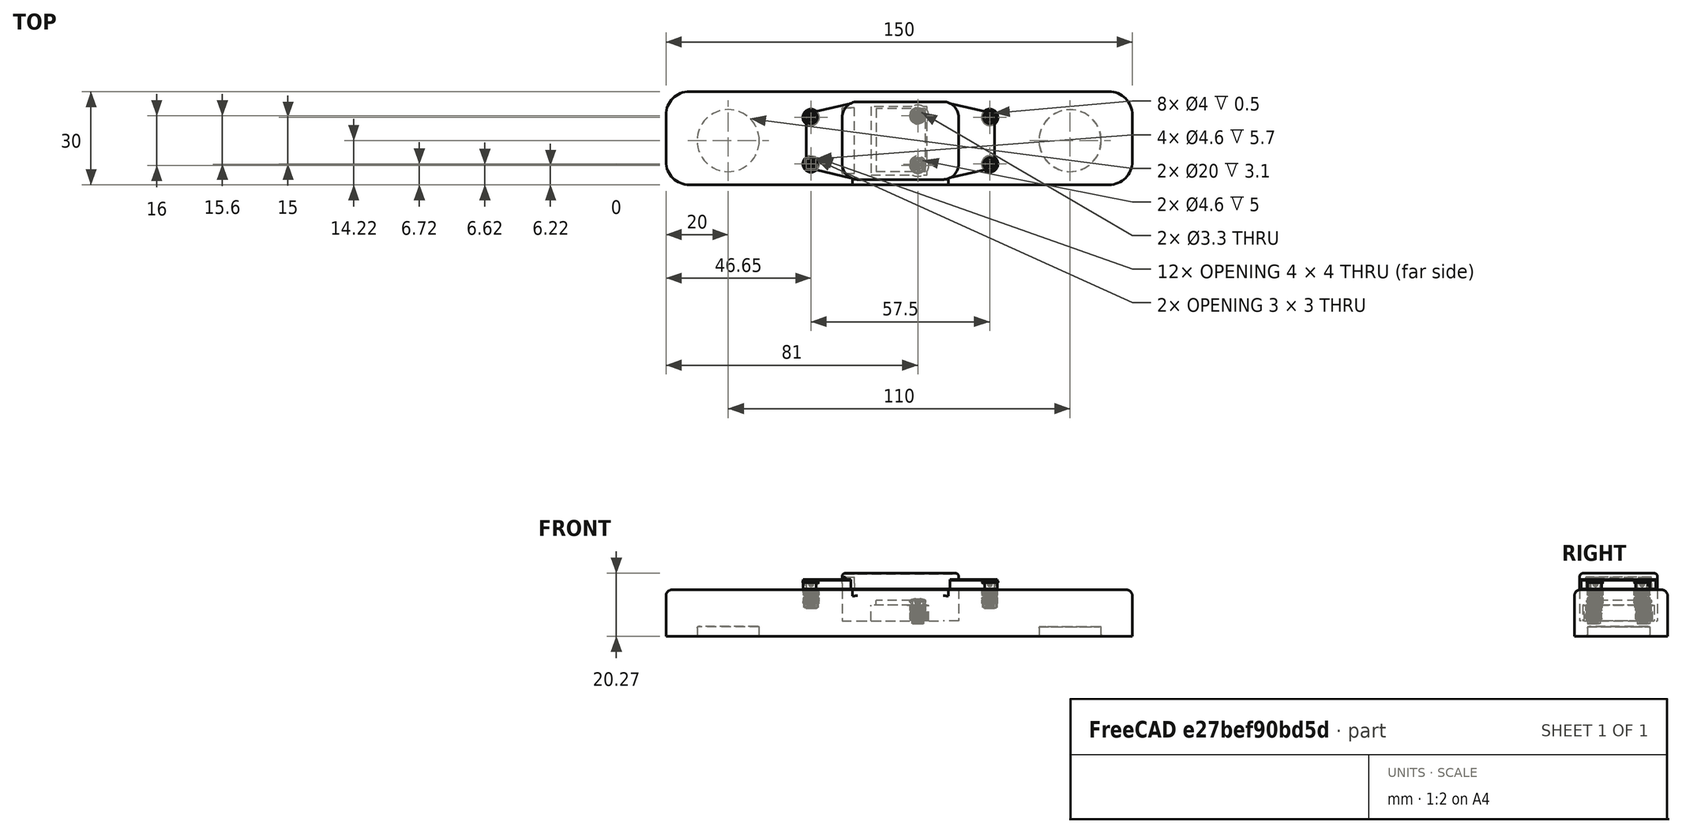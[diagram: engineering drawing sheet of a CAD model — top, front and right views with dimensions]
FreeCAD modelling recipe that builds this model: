
FCSTD DOCUMENT  (FreeCAD 0.20R29603 (Git))
Label: MMI Assembly
License: All rights reserved
LicenseURL: http://en.wikipedia.org/wiki/All_rights_reserved
objects: App::FeaturePython×30, Part::FeaturePython×18
note: 18 computed .brp shape members not serialized (recipe doc carries the construction recipe); baked Part::Feature solids carry a one-line shape summary decoded from their .brp

FEATURE [Part::FeaturePython] b_Sensor_Holder_001_  label="Sensor Holder_001"  # a2plus imported part (geometry in sourceFile) (typed FeaturePython)
  a2p_Version = 0.4.60n
  fixedPosition = true
  objectType = a2pPart
  sourceFile = .\Sensor Holder.FCStd
  subassemblyImport = false
  timeLastImport = 1.68601e+09
  updateColors = true
FEATURE [Part::FeaturePython] b_M3_Heat_Insert_001_  label="M3 Heat Insert_001"  # a2plus imported part (geometry in sourceFile) (typed FeaturePython)
  Placement = pos=(6.00013,7.99989,4) rot=(0,0,1;0rad)
  a2p_Version = 0.4.60n
  fixedPosition = false
  objectType = a2pPart
  sourceFile = .\M3 Heat Insert.FCStd
  subassemblyImport = false
  timeLastImport = 1.68601e+09
  updateColors = true
FEATURE [App::FeaturePython] centerOfMass_001  label="centerOfMass_001__M3 Heat Insert_001"  # a2plus constraint (typed FeaturePython)
  Object1 = b_Sensor_Holder_001_
  Object2 = b_M3_Heat_Insert_001_
  ParentTreeObject = -> b_Sensor_Holder_001_
  SubElement1 = Edge144
  SubElement2 = Edge31
  Suppressed = false
  Type = CenterOfMass
  directionConstraint = 0
  lockRotation = false
  offset = 0
FEATURE [App::FeaturePython] centerOfMass_001_mirror  label="centerOfMass_001__Sensor Holder_001"  # a2plus constraint (typed FeaturePython)
  Object1 = b_Sensor_Holder_001_
  Object2 = b_M3_Heat_Insert_001_
  ParentTreeObject = -> b_M3_Heat_Insert_001_
  SubElement1 = Edge144
  SubElement2 = Edge31
  Suppressed = false
  Type = CenterOfMass
  directionConstraint = 0
  lockRotation = false
  offset = 0
FEATURE [Part::FeaturePython] b_M3_Heat_Insert_001_001  label="M3 Heat Insert_002"  # a2plus imported part (geometry in sourceFile) (typed FeaturePython)
  Placement = pos=(6.00013,-8.00011,4) rot=(0,0,1;0rad)
  a2p_Version = 0.4.60n
  fixedPosition = false
  objectType = a2pPart
  sourceFile = .\M3 Heat Insert.FCStd
  subassemblyImport = false
  timeLastImport = 1.68601e+09
  updateColors = true
FEATURE [App::FeaturePython] centerOfMass_002  label="centerOfMass_002__Sensor Holder_001"  # a2plus constraint (typed FeaturePython)
  Object1 = b_M3_Heat_Insert_001_001
  Object2 = b_Sensor_Holder_001_
  ParentTreeObject = -> b_M3_Heat_Insert_001_001
  SubElement1 = Edge31
  SubElement2 = Edge145
  Suppressed = false
  Type = CenterOfMass
  directionConstraint = 0
  lockRotation = false
  offset = 0
FEATURE [App::FeaturePython] centerOfMass_002_mirror  label="centerOfMass_002__M3 Heat Insert_002"  # a2plus constraint (typed FeaturePython)
  Object1 = b_M3_Heat_Insert_001_001
  Object2 = b_Sensor_Holder_001_
  ParentTreeObject = -> b_Sensor_Holder_001_
  SubElement1 = Edge31
  SubElement2 = Edge145
  Suppressed = false
  Type = CenterOfMass
  directionConstraint = 0
  lockRotation = false
  offset = 0
FEATURE [Part::FeaturePython] b_M3_Heat_Insert_001_002  label="M3 Heat Insert_003"  # a2plus imported part (geometry in sourceFile) (typed FeaturePython)
  Placement = pos=(-28.3499,7.49989,9) rot=(0,0,1;0rad)
  a2p_Version = 0.4.60n
  fixedPosition = false
  objectType = a2pPart
  sourceFile = .\M3 Heat Insert.FCStd
  subassemblyImport = false
  timeLastImport = 1.68601e+09
  updateColors = true
FEATURE [App::FeaturePython] centerOfMass_003  label="centerOfMass_003__Sensor Holder_001"  # a2plus constraint (typed FeaturePython)
  Object1 = b_M3_Heat_Insert_001_002
  Object2 = b_Sensor_Holder_001_
  ParentTreeObject = -> b_M3_Heat_Insert_001_002
  SubElement1 = Edge31
  SubElement2 = Edge19
  Suppressed = false
  Type = CenterOfMass
  directionConstraint = 0
  lockRotation = false
  offset = 0
FEATURE [App::FeaturePython] centerOfMass_003_mirror  label="centerOfMass_003__M3 Heat Insert_003"  # a2plus constraint (typed FeaturePython)
  Object1 = b_M3_Heat_Insert_001_002
  Object2 = b_Sensor_Holder_001_
  ParentTreeObject = -> b_Sensor_Holder_001_
  SubElement1 = Edge31
  SubElement2 = Edge19
  Suppressed = false
  Type = CenterOfMass
  directionConstraint = 0
  lockRotation = false
  offset = 0
FEATURE [Part::FeaturePython] b_M3_Heat_Insert_001_003  label="M3 Heat Insert_004"  # a2plus imported part (geometry in sourceFile) (typed FeaturePython)
  Placement = pos=(-28.3499,-7.50011,9) rot=(0,0,1;0rad)
  a2p_Version = 0.4.60n
  fixedPosition = false
  objectType = a2pPart
  sourceFile = .\M3 Heat Insert.FCStd
  subassemblyImport = false
  timeLastImport = 1.68601e+09
  updateColors = true
FEATURE [Part::FeaturePython] b_M3_Heat_Insert_001_004  label="M3 Heat Insert_005"  # a2plus imported part (geometry in sourceFile) (typed FeaturePython)
  Placement = pos=(29.1501,-7.50011,9) rot=(0,0,1;0rad)
  a2p_Version = 0.4.60n
  fixedPosition = false
  objectType = a2pPart
  sourceFile = .\M3 Heat Insert.FCStd
  subassemblyImport = false
  timeLastImport = 1.68601e+09
  updateColors = true
FEATURE [App::FeaturePython] centerOfMass_005  label="centerOfMass_005__Sensor Holder_001"  # a2plus constraint (typed FeaturePython)
  Object1 = b_M3_Heat_Insert_001_004
  Object2 = b_Sensor_Holder_001_
  ParentTreeObject = -> b_M3_Heat_Insert_001_004
  SubElement1 = Edge31
  SubElement2 = Edge18
  Suppressed = false
  Type = CenterOfMass
  directionConstraint = 0
  lockRotation = false
  offset = 0
FEATURE [App::FeaturePython] centerOfMass_005_mirror  label="centerOfMass_005__M3 Heat Insert_005"  # a2plus constraint (typed FeaturePython)
  Object1 = b_M3_Heat_Insert_001_004
  Object2 = b_Sensor_Holder_001_
  ParentTreeObject = -> b_Sensor_Holder_001_
  SubElement1 = Edge31
  SubElement2 = Edge18
  Suppressed = false
  Type = CenterOfMass
  directionConstraint = 0
  lockRotation = false
  offset = 0
FEATURE [Part::FeaturePython] b_M3_Heat_Insert_001_005  label="M3 Heat Insert_006"  # a2plus imported part (geometry in sourceFile) (typed FeaturePython)
  Placement = pos=(29.1501,7.49989,9) rot=(0,0,1;0rad)
  a2p_Version = 0.4.60n
  fixedPosition = false
  objectType = a2pPart
  sourceFile = .\M3 Heat Insert.FCStd
  subassemblyImport = false
  timeLastImport = 1.68601e+09
  updateColors = true
FEATURE [App::FeaturePython] centerOfMass_006  label="centerOfMass_006__Sensor Holder_001"  # a2plus constraint (typed FeaturePython)
  Object1 = b_M3_Heat_Insert_001_005
  Object2 = b_Sensor_Holder_001_
  ParentTreeObject = -> b_M3_Heat_Insert_001_005
  SubElement1 = Edge31
  SubElement2 = Edge20
  Suppressed = false
  Type = CenterOfMass
  directionConstraint = 0
  lockRotation = false
  offset = 0
FEATURE [App::FeaturePython] centerOfMass_006_mirror  label="centerOfMass_006__M3 Heat Insert_006"  # a2plus constraint (typed FeaturePython)
  Object1 = b_M3_Heat_Insert_001_005
  Object2 = b_Sensor_Holder_001_
  ParentTreeObject = -> b_Sensor_Holder_001_
  SubElement1 = Edge31
  SubElement2 = Edge20
  Suppressed = false
  Type = CenterOfMass
  directionConstraint = 0
  lockRotation = false
  offset = 0
FEATURE [Part::FeaturePython] b_Sensor_Holder_Cap_001_  label="Sensor Holder Cap_001"  # a2plus imported part (geometry in sourceFile) (typed FeaturePython)
  Placement = pos=(0.4,9.94825e-09,15.2703) rot=(0,0,1;0rad)
  a2p_Version = 0.4.60n
  fixedPosition = false
  objectType = a2pPart
  sourceFile = .\Sensor Holder Cap.FCStd
  subassemblyImport = false
  timeLastImport = 1.68601e+09
  updateColors = true
FEATURE [App::FeaturePython] axisCoincident_001  label="axisCoincident_001__Sensor Holder Cap_001"  # a2plus constraint (typed FeaturePython)
  Object1 = b_Sensor_Holder_001_
  Object2 = b_Sensor_Holder_Cap_001_
  ParentTreeObject = -> b_Sensor_Holder_001_
  SubElement1 = Edge17
  SubElement2 = Edge148
  Suppressed = false
  Type = axial
  directionConstraint = 0
  lockRotation = false
FEATURE [App::FeaturePython] axisCoincident_001_mirror  label="axisCoincident_001__Sensor Holder_001"  # a2plus constraint (typed FeaturePython)
  Object1 = b_Sensor_Holder_001_
  Object2 = b_Sensor_Holder_Cap_001_
  ParentTreeObject = -> b_Sensor_Holder_Cap_001_
  SubElement1 = Edge17
  SubElement2 = Edge148
  Suppressed = false
  Type = axial
  directionConstraint = 0
  lockRotation = false
FEATURE [Part::FeaturePython] b_MPU6050_PCBA_001_  label="MPU6050_PCBA_Body_001"  # a2plus imported part (geometry in sourceFile) (typed FeaturePython)
  Placement = pos=(0.8,0.2,10) rot=(0,0,-1;1.5708rad)
  a2p_Version = 0.4.60n
  fixedPosition = false
  objectType = a2pPart
  sourceFile = .\MPU6050_PCBA.FCStd
  sourcePart = Body
  subassemblyImport = false
  timeLastImport = 1.68601e+09
  updateColors = true
FEATURE [App::FeaturePython] centerOfMass_004  label="centerOfMass_004__M3 Heat Insert_001"  # a2plus constraint (typed FeaturePython)
  Object1 = b_MPU6050_PCBA_001_
  Object2 = b_M3_Heat_Insert_001_
  ParentTreeObject = -> b_MPU6050_PCBA_001_
  SubElement1 = Edge12
  SubElement2 = Edge31
  Suppressed = false
  Type = CenterOfMass
  directionConstraint = 0
  lockRotation = false
  offset = 0
FEATURE [App::FeaturePython] centerOfMass_004_mirror  label="centerOfMass_004__MPU6050_PCBA_Body_001"  # a2plus constraint (typed FeaturePython)
  Object1 = b_MPU6050_PCBA_001_
  Object2 = b_M3_Heat_Insert_001_
  ParentTreeObject = -> b_M3_Heat_Insert_001_
  SubElement1 = Edge12
  SubElement2 = Edge31
  Suppressed = false
  Type = CenterOfMass
  directionConstraint = 0
  lockRotation = false
  offset = 0
FEATURE [Part::FeaturePython] Screw  label="M3x5-Screw"  # Fasteners workbench fastener (typed FeaturePython)
  Placement = pos=(6,8,11.5) rot=(0,0,1;0rad)
  baseObject = -> b_MPU6050_PCBA_001_ [Edge15]
  diameter = 4
  invert = false
  leftHanded = false
  length = 1
  lengthCustom = 5
  matchOuter = false
  offset = 0
  thread = false
  type = 48
FEATURE [Part::FeaturePython] Screw001  label="M3x6-Screw"  # Fasteners workbench fastener (typed FeaturePython)
  Placement = pos=(6,-7.6,11.5) rot=(0,0,1;0rad)
  baseObject = -> b_MPU6050_PCBA_001_ [Edge16]
  diameter = 4
  invert = false
  leftHanded = false
  length = 2
  lengthCustom = 6
  matchOuter = false
  offset = 0
  thread = false
  type = 48
FEATURE [Part::FeaturePython] Screw006  label="M3x5-Screw005"  # Fasteners workbench fastener (typed FeaturePython)
  Placement = pos=(-28.35,-7.5,17.7703) rot=(0,0,1;0rad)
  baseObject = -> b_Sensor_Holder_Cap_001_ [Edge155]
  diameter = 4
  invert = true
  leftHanded = false
  length = 1
  lengthCustom = 5
  matchOuter = false
  offset = 0
  thread = false
  type = 48
FEATURE [Part::FeaturePython] Screw008  label="M3x5-Screw006"  # Fasteners workbench fastener (typed FeaturePython)
  Placement = pos=(29.15,-7.5,17.7703) rot=(0,0,1;0rad)
  baseObject = -> b_Sensor_Holder_Cap_001_ [Edge143]
  diameter = 4
  invert = true
  leftHanded = false
  length = 1
  lengthCustom = 5
  matchOuter = false
  offset = 0
  thread = false
  type = 48
FEATURE [Part::FeaturePython] Screw009  label="M3x5-Screw007"  # Fasteners workbench fastener (typed FeaturePython)
  Placement = pos=(29.15,7.5,17.7703) rot=(0,0,1;0rad)
  baseObject = -> b_Sensor_Holder_Cap_001_ [Edge133]
  diameter = 4
  invert = true
  leftHanded = false
  length = 1
  lengthCustom = 5
  matchOuter = false
  offset = 0
  thread = false
  type = 48
FEATURE [Part::FeaturePython] Screw010  label="M3x5-Screw004"  # Fasteners workbench fastener (typed FeaturePython)
  Placement = pos=(-28.3497,7.5,17.7703) rot=(0,0,1;0rad)
  baseObject = -> b_Sensor_Holder_Cap_001_ [Edge186]
  diameter = 4
  invert = true
  leftHanded = false
  length = 1
  lengthCustom = 5
  matchOuter = false
  offset = 0
  thread = false
  type = 48
FEATURE [Part::FeaturePython] b_Sensor_Holder_Cap_WH_001_  label="Sensor Holder Cap WH_001"  # a2plus imported part (geometry in sourceFile) (typed FeaturePython)
  Placement = pos=(0.4,0,15) rot=(0,0,1;0rad)
  a2p_Version = 0.4.60n
  fixedPosition = false
  objectType = a2pPart
  sourceFile = .\Sensor Holder Cap WH.FCStd
  subassemblyImport = false
  timeLastImport = 1.68602e+09
  updateColors = true
FEATURE [App::FeaturePython] planesParallel_001  label="planesParallel_001__Sensor Holder Cap WH_001"  # a2plus constraint (typed FeaturePython)
  Object1 = b_M3_Heat_Insert_001_003
  Object2 = b_Sensor_Holder_Cap_WH_001_
  ParentTreeObject = -> b_M3_Heat_Insert_001_003
  SubElement1 = Face1
  SubElement2 = Face83
  Suppressed = false
  Type = planesParallel
  directionConstraint = 0
FEATURE [App::FeaturePython] planesParallel_001_mirror  label="planesParallel_001__M3 Heat Insert_004"  # a2plus constraint (typed FeaturePython)
  Object1 = b_M3_Heat_Insert_001_003
  Object2 = b_Sensor_Holder_Cap_WH_001_
  ParentTreeObject = -> b_Sensor_Holder_Cap_WH_001_
  SubElement1 = Face1
  SubElement2 = Face83
  Suppressed = false
  Type = planesParallel
  directionConstraint = 0
FEATURE [App::FeaturePython] axisCoincident_002  label="axisCoincident_002__Sensor Holder_001"  # a2plus constraint (typed FeaturePython)
  Object1 = b_Sensor_Holder_Cap_WH_001_
  Object2 = b_Sensor_Holder_001_
  ParentTreeObject = -> b_Sensor_Holder_Cap_WH_001_
  SubElement1 = Edge96
  SubElement2 = Edge20
  Suppressed = false
  Type = axial
  directionConstraint = 0
  lockRotation = false
FEATURE [App::FeaturePython] axisCoincident_002_mirror  label="axisCoincident_002__Sensor Holder Cap WH_001"  # a2plus constraint (typed FeaturePython)
  Object1 = b_Sensor_Holder_Cap_WH_001_
  Object2 = b_Sensor_Holder_001_
  ParentTreeObject = -> b_Sensor_Holder_001_
  SubElement1 = Edge96
  SubElement2 = Edge20
  Suppressed = false
  Type = axial
  directionConstraint = 0
  lockRotation = false
FEATURE [App::FeaturePython] pointIdentity_001  label="pointIdentity_001__Sensor Holder_001"  # a2plus constraint (typed FeaturePython)
  Object1 = b_Sensor_Holder_Cap_WH_001_
  Object2 = b_Sensor_Holder_001_
  ParentTreeObject = -> b_Sensor_Holder_Cap_WH_001_
  SubElement1 = Edge140
  SubElement2 = Edge20
  Suppressed = false
  Type = pointIdentity
FEATURE [App::FeaturePython] pointIdentity_001_mirror  label="pointIdentity_001__Sensor Holder Cap WH_001"  # a2plus constraint (typed FeaturePython)
  Object1 = b_Sensor_Holder_Cap_WH_001_
  Object2 = b_Sensor_Holder_001_
  ParentTreeObject = -> b_Sensor_Holder_001_
  SubElement1 = Edge140
  SubElement2 = Edge20
  Suppressed = false
  Type = pointIdentity
FEATURE [Part::FeaturePython] b_Nedymium_Magnet_OD20mm_H3mm_001_  label="Nedymium Magnet OD20mm H3mm_001"  # a2plus imported part (geometry in sourceFile) (typed FeaturePython)
  Placement = pos=(-55,7.33426e-10,0.12) rot=(0,0,1;0rad)
  a2p_Version = 0.4.60n
  fixedPosition = false
  objectType = a2pPart
  sourceFile = .\Nedymium Magnet OD20mm H3mm.FCStd
  subassemblyImport = false
  timeLastImport = 1.6863e+09
  updateColors = true
FEATURE [App::FeaturePython] axisCoincident_003  label="axisCoincident_003__Sensor Holder_001"  # a2plus constraint (typed FeaturePython)
  Object1 = b_Nedymium_Magnet_OD20mm_H3mm_001_
  Object2 = b_Sensor_Holder_001_
  ParentTreeObject = -> b_Nedymium_Magnet_OD20mm_H3mm_001_
  SubElement1 = Edge2
  SubElement2 = Face61
  Suppressed = false
  Type = axial
  directionConstraint = 1
  lockRotation = false
FEATURE [App::FeaturePython] axisCoincident_003_mirror  label="axisCoincident_003__Nedymium Magnet OD20mm H3mm_001"  # a2plus constraint (typed FeaturePython)
  Object1 = b_Nedymium_Magnet_OD20mm_H3mm_001_
  Object2 = b_Sensor_Holder_001_
  ParentTreeObject = -> b_Sensor_Holder_001_
  SubElement1 = Edge2
  SubElement2 = Face61
  Suppressed = false
  Type = axial
  directionConstraint = 1
  lockRotation = false
FEATURE [App::FeaturePython] pointIdentity_002  label="pointIdentity_002__Sensor Holder_001"  # a2plus constraint (typed FeaturePython)
  Object1 = b_Nedymium_Magnet_OD20mm_H3mm_001_
  Object2 = b_Sensor_Holder_001_
  ParentTreeObject = -> b_Nedymium_Magnet_OD20mm_H3mm_001_
  SubElement1 = Edge3
  SubElement2 = Edge141
  Suppressed = false
  Type = pointIdentity
FEATURE [App::FeaturePython] pointIdentity_002_mirror  label="pointIdentity_002__Nedymium Magnet OD20mm H3mm_001"  # a2plus constraint (typed FeaturePython)
  Object1 = b_Nedymium_Magnet_OD20mm_H3mm_001_
  Object2 = b_Sensor_Holder_001_
  ParentTreeObject = -> b_Sensor_Holder_001_
  SubElement1 = Edge3
  SubElement2 = Edge141
  Suppressed = false
  Type = pointIdentity
FEATURE [Part::FeaturePython] b_Nedymium_Magnet_OD20mm_H3mm_001_001  label="Nedymium Magnet OD20mm H3mm_002"  # a2plus imported part (geometry in sourceFile) (typed FeaturePython)
  Placement = pos=(55,-2.32187e-08,0.100006) rot=(0,0,1;0rad)
  a2p_Version = 0.4.60n
  fixedPosition = false
  objectType = a2pPart
  sourceFile = .\Nedymium Magnet OD20mm H3mm.FCStd
  subassemblyImport = false
  timeLastImport = 1.6863e+09
  updateColors = true
FEATURE [App::FeaturePython] axisCoincident_004  label="axisCoincident_004__Sensor Holder_001"  # a2plus constraint (typed FeaturePython)
  Object1 = b_Nedymium_Magnet_OD20mm_H3mm_001_001
  Object2 = b_Sensor_Holder_001_
  ParentTreeObject = -> b_Nedymium_Magnet_OD20mm_H3mm_001_001
  SubElement1 = Face1
  SubElement2 = Face62
  Suppressed = false
  Type = axial
  directionConstraint = 0
  lockRotation = false
FEATURE [App::FeaturePython] axisCoincident_004_mirror  label="axisCoincident_004__Nedymium Magnet OD20mm H3mm_002"  # a2plus constraint (typed FeaturePython)
  Object1 = b_Nedymium_Magnet_OD20mm_H3mm_001_001
  Object2 = b_Sensor_Holder_001_
  ParentTreeObject = -> b_Sensor_Holder_001_
  SubElement1 = Face1
  SubElement2 = Face62
  Suppressed = false
  Type = axial
  directionConstraint = 0
  lockRotation = false
FEATURE [App::FeaturePython] pointOnPlane_001  label="pointOnPlane_001__Sensor Holder_001"  # a2plus constraint (typed FeaturePython)
  Object1 = b_Nedymium_Magnet_OD20mm_H3mm_001_001
  Object2 = b_Sensor_Holder_001_
  ParentTreeObject = -> b_Nedymium_Magnet_OD20mm_H3mm_001_001
  SubElement1 = Edge7
  SubElement2 = Face66
  Suppressed = false
  Type = pointOnPlane
  offset = 0
FEATURE [App::FeaturePython] pointOnPlane_001_mirror  label="pointOnPlane_001__Nedymium Magnet OD20mm H3mm_002"  # a2plus constraint (typed FeaturePython)
  Object1 = b_Nedymium_Magnet_OD20mm_H3mm_001_001
  Object2 = b_Sensor_Holder_001_
  ParentTreeObject = -> b_Sensor_Holder_001_
  SubElement1 = Edge7
  SubElement2 = Face66
  Suppressed = false
  Type = pointOnPlane
  offset = 0
FEATURE [App::FeaturePython] planeCoincident_001  label="planeCoincident_001__Sensor Holder_001"  # a2plus constraint (typed FeaturePython)
  Object1 = b_Nedymium_Magnet_OD20mm_H3mm_001_
  Object2 = b_Sensor_Holder_001_
  ParentTreeObject = -> b_Nedymium_Magnet_OD20mm_H3mm_001_
  SubElement1 = Face4
  SubElement2 = Face53
  Suppressed = false
  Type = plane
  directionConstraint = 0
  offset = 0
FEATURE [App::FeaturePython] planeCoincident_001_mirror  label="planeCoincident_001__Nedymium Magnet OD20mm H3mm_001"  # a2plus constraint (typed FeaturePython)
  Object1 = b_Nedymium_Magnet_OD20mm_H3mm_001_
  Object2 = b_Sensor_Holder_001_
  ParentTreeObject = -> b_Sensor_Holder_001_
  SubElement1 = Face4
  SubElement2 = Face53
  Suppressed = false
  Type = plane
  directionConstraint = 0
  offset = 0
